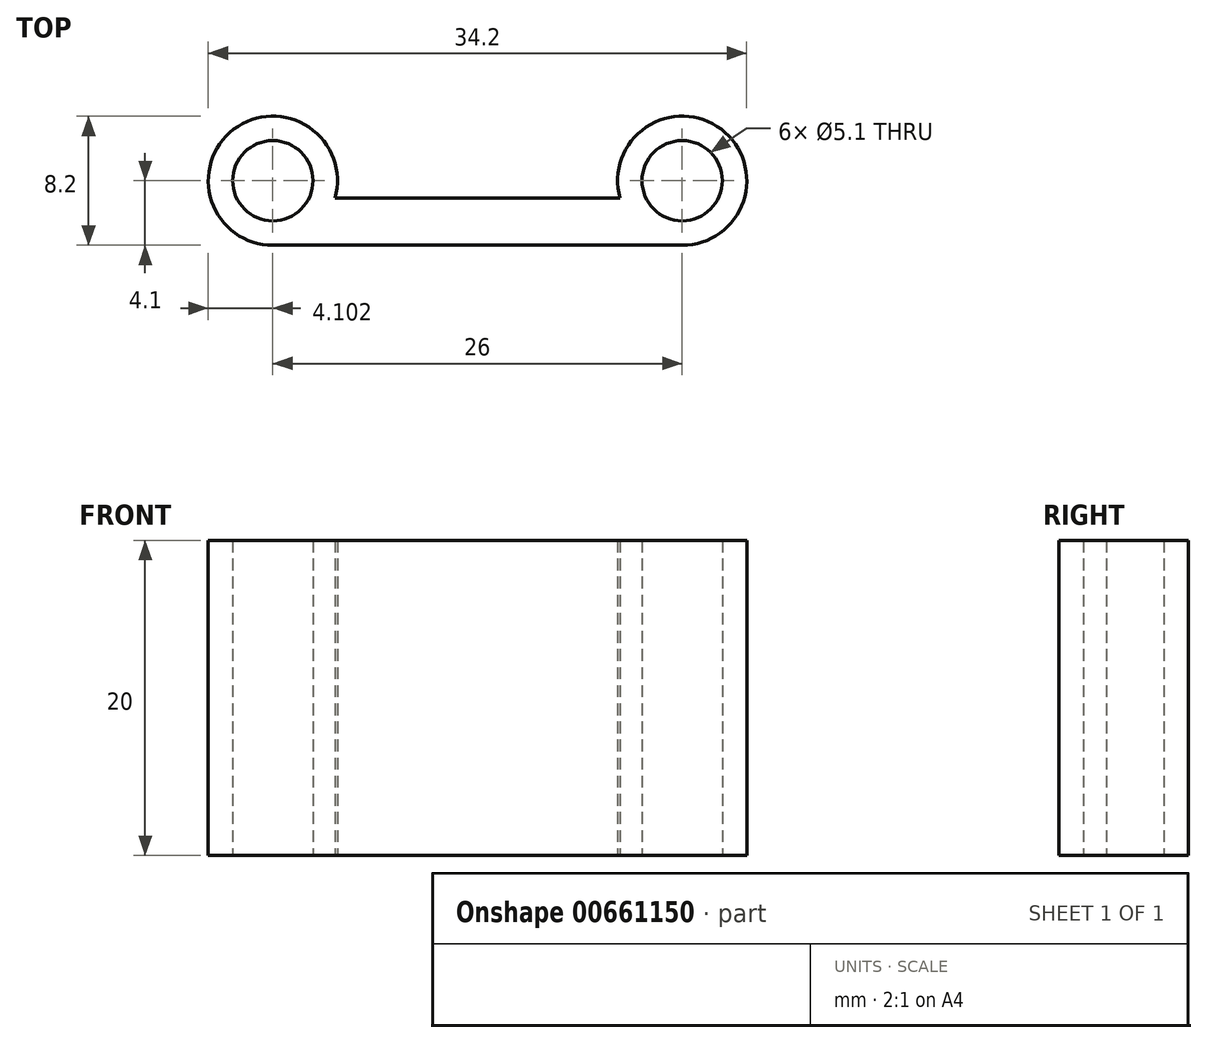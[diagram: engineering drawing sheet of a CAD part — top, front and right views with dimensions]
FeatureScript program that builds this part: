
annotation { "Feature Type Name" : "Feature", "Feature Type Description" : "" }
export const myFeature = defineFeature(function(context is Context, id is Id, definition is map)
    precondition{}
    {
        {
            var Q0;
            Q0=qCreatedBy(makeId("Top.planeOp"),FACE);
            var sketch = newSketch(context, id + "F0", { "sketchPlane" : qUnion([Q0])});
            skCircle(sketch, "E0", {"center": v(7.31, 0) * mm, "radius": 2.55 * mm});
            skCircle(sketch, "E1", {"center": v(-18.69, 0) * mm, "radius": 2.55 * mm});
            skArc(sketch, "E2", {"start": v(-14.74, -1.1) * mm, "mid": v(-21.17, 3.26) * mm, "end": v(-18.69, -4.1) * mm});
            skArc(sketch, "E3", {"start": v(7.31, -4.1) * mm, "mid": v(9.8, 3.26) * mm, "end": v(3.36, -1.1) * mm});
            skLineSegment(sketch, "E4", {"start": v(-18.69, -4.1) * mm, "end": v(7.31, -4.1) * mm});
            skLineSegment(sketch, "E5.0", {"start": v(-14.74, -1.1) * mm, "end": v(3.36, -1.1) * mm});
            skSolve(sketch);
        }
        {
            var Q0;
            Q0=makeQuery(id+"F0.imprint","IMPRINT",FACE,{"disambiguationData":[TD([[makeQuery(id+"F0.imprint","IMPRINT",EDGE,{"derivedFrom":sQuery(id+"F0.wireOp",EDGE,"E0")}),-1.0]])]});
            extrude(context, id + "F1", {"entities" : qUnion([Q0]), "depth" : 20 * mm, "offsetDistance" : 25 * mm});
        }
    });
